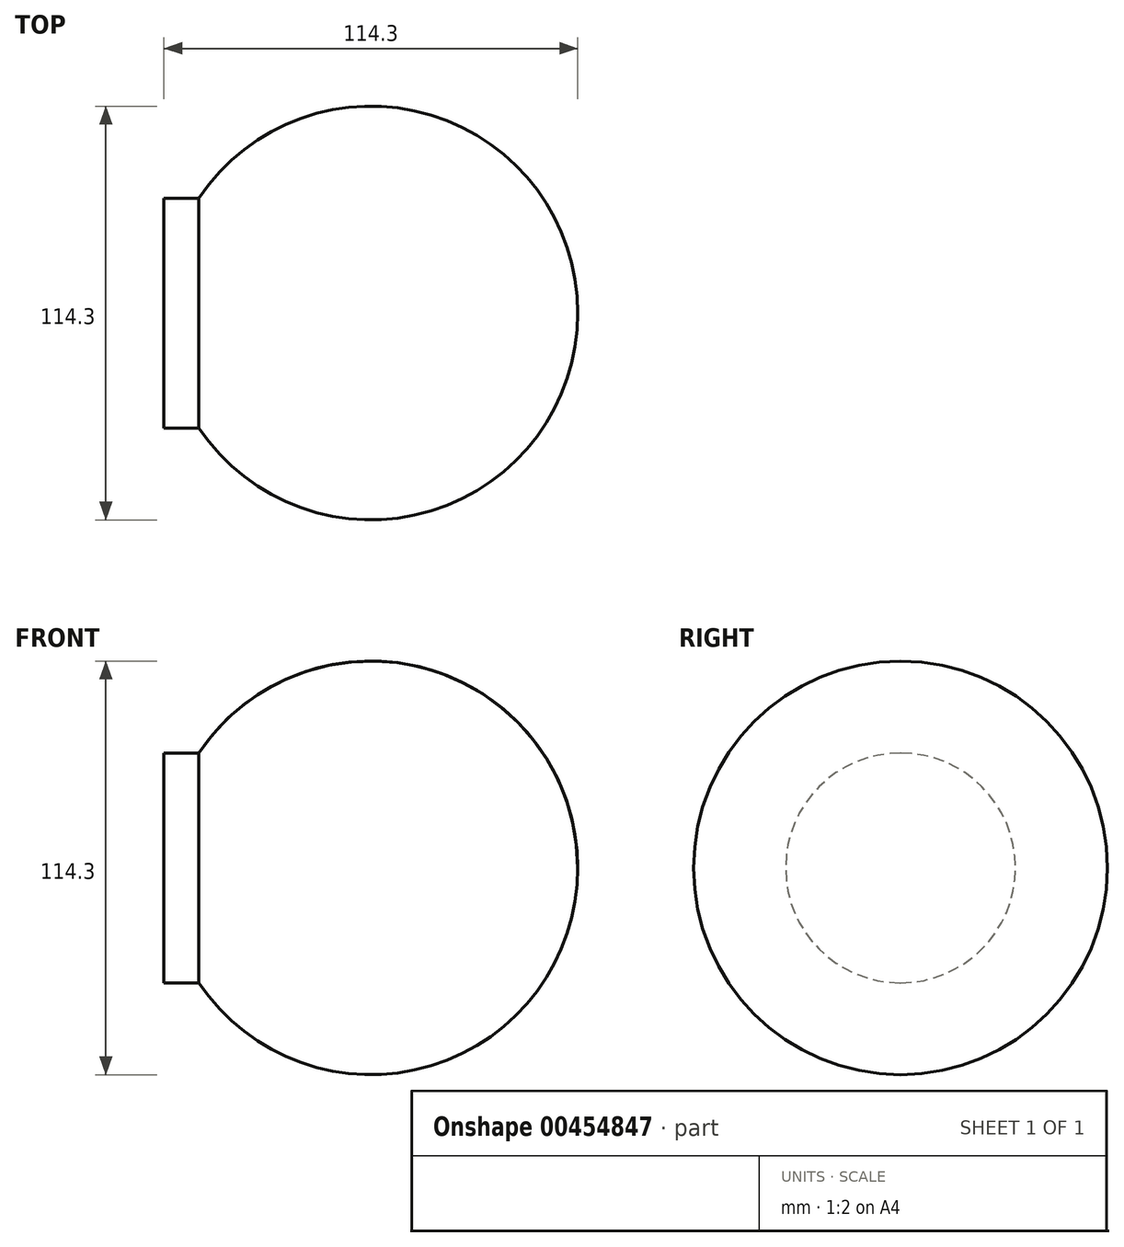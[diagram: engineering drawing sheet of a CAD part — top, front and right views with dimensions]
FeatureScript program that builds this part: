
annotation { "Feature Type Name" : "Feature", "Feature Type Description" : "" }
export const myFeature = defineFeature(function(context is Context, id is Id, definition is map)
    precondition{}
    {
        {
            var Q0;
            Q0=qCreatedBy(makeId("Right.planeOp"),FACE);
            var sketch = newSketch(context, id + "F0", { "sketchPlane" : qUnion([Q0])});
            skCircle(sketch, "E0", {"center": v(0, 0) * mm, "radius": 57.15 * mm});
            skSolve(sketch);
        }
        {
            var Q0;
            Q0 = qSketchRegion(id + "F0", true);
            extrude(context, id + "F1", {"entities" : qUnion([Q0]), "depth" : 57.15 * mm, "offsetDistance" : 25.4 * mm});
        }
        {
            var Q0;
            Q0=makeQuery(id+"F1.opExtrude","CAP_FACE",FACE,{"disambiguationData":[OSD([sQuery(id+"F0.wireOp",EDGE,"E0")])],"isStart":true});
            var sketch = newSketch(context, id + "F2", { "sketchPlane" : qUnion([Q0])});
            skCircle(sketch, "E1", {"center": v(0, 0) * mm, "radius": 57.15 * mm});
            skSolve(sketch);
        }
        {
            var Q0;
            Q0 = qSketchRegion(id + "F2", true);
            extrude(context, id + "F3", {"entities" : qUnion([Q0]), "operationType" : NewBodyOperationType.ADD, "depth" : 57.15 * mm, "offsetDistance" : 25.4 * mm});
        }
        {
            var Q0;
            Q0=makeQuery(id+"F3.opExtrude","CAP_EDGE",EDGE,{"disambiguationData":[OSD([sQuery(id+"F2.wireOp",EDGE,"E1")])],"isStart":false});
            fillet(context, id + "F4", {"entities" : qUnion([Q0]), "radius" : 57.15 * mm, "tangentPropagation" : true, "allowEdgeOverflow" : false});
        }
        {
            var Q0;
            Q0=makeQuery(id+"F1.opExtrude","CAP_EDGE",EDGE,{"disambiguationData":[OSD([sQuery(id+"F0.wireOp",EDGE,"E0")])],"isStart":false});
            fillet(context, id + "F5", {"entities" : qUnion([Q0]), "radius" : 57.15 * mm, "tangentPropagation" : true, "allowEdgeOverflow" : false});
        }
        {
            var Q0;
            Q0=makeQuery(id+"F2.imprint","IMPRINT",FACE,{"disambiguationData":[TD([[makeQuery(id+"F2.imprint","IMPRINT",EDGE,{"derivedFrom":sQuery(id+"F2.wireOp",EDGE,"E1")}),-1.0]])]});
            var sketch = newSketch(context, id + "F6", { "sketchPlane" : qUnion([Q0])});
            skCircle(sketch, "E2", {"center": v(0, 0) * mm, "radius": 31.75 * mm});
            skSolve(sketch);
        }
        {
            var Q0;
            Q0 = qSketchRegion(id + "F6", true);
            extrude(context, id + "F7", {"entities" : qUnion([Q0]), "operationType" : NewBodyOperationType.ADD, "depth" : 57.15 * mm, "offsetDistance" : 25.4 * mm});
        }
    });
